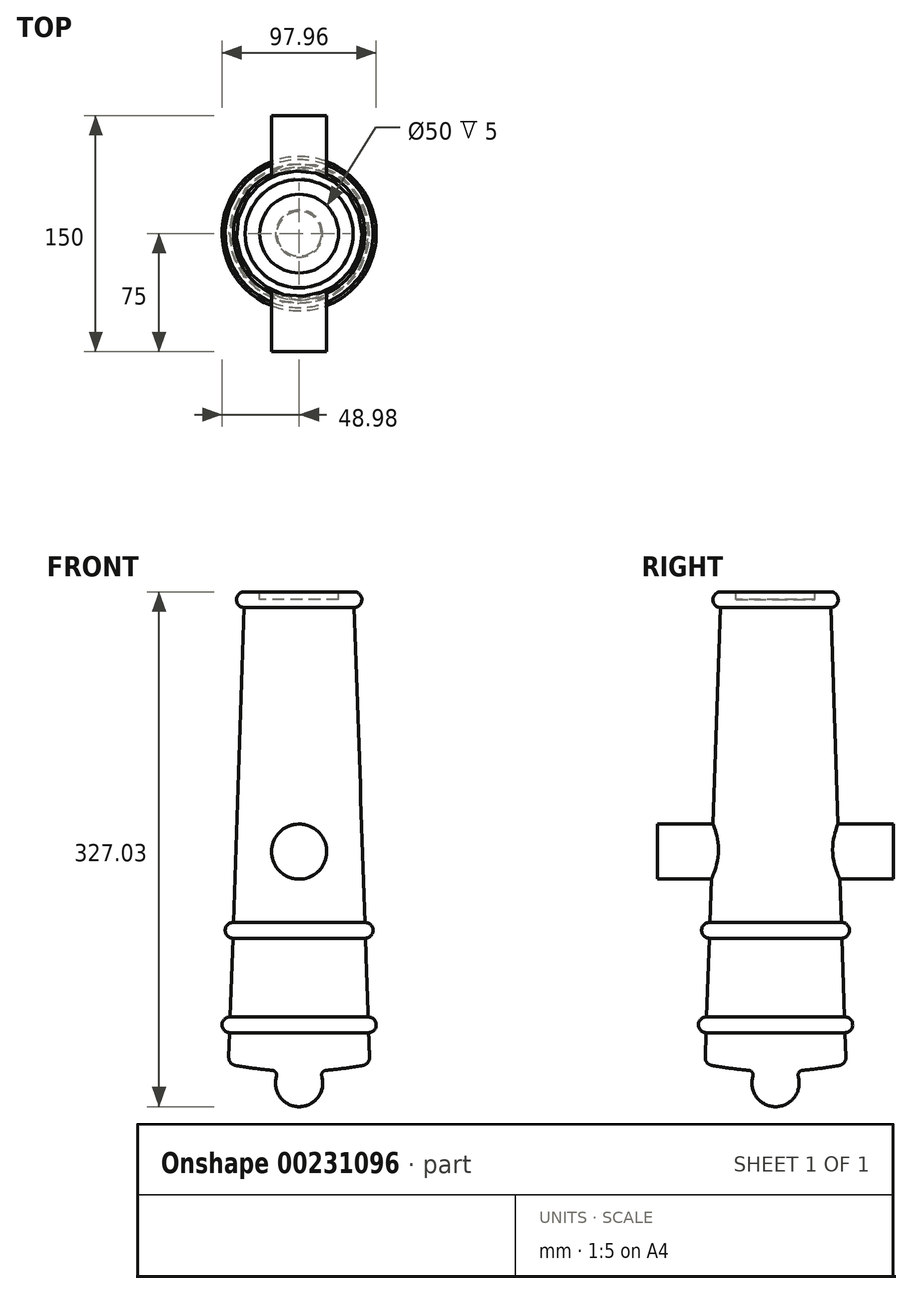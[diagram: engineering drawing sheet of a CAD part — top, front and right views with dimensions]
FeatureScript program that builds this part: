
annotation { "Feature Type Name" : "Feature", "Feature Type Description" : "" }
export const myFeature = defineFeature(function(context is Context, id is Id, definition is map)
    precondition{}
    {
        {
            var Q0;
            Q0=qCreatedBy(makeId("Front.planeOp"),FACE);
            var sketch = newSketch(context, id + "F0", { "sketchPlane" : qUnion([Q0])});
            skLineSegment(sketch, "E0", {"start": v(0, 300) * mm, "end": v(25, 300) * mm});
            skLineSegment(sketch, "E1", {"start": v(25, 300) * mm, "end": v(25, 305) * mm});
            skLineSegment(sketch, "E2", {"start": v(35, 295.03) * mm, "end": v(44.68, 9.3) * mm});
            skArc(sketch, "E3", {"start": v(17, 1.05) * mm, "mid": v(28.81, 2.39) * mm, "end": v(40.56, 4.21) * mm});
            skPoint(sketch, "E4.orphan", {"position": v(45, 0) * mm});
            skPoint(sketch, "E5.visualSharp", {"position": v(44.83, 5) * mm});
            skArc(sketch, "E5.filletArc", {"start": v(40.56, 4.21) * mm, "mid": v(43.57, 5.99) * mm, "end": v(44.68, 9.3) * mm});
            skLineSegment(sketch, "E6", {"start": v(0, 300) * mm, "end": v(0, 0) * mm});
            skCircle(sketch, "E7", {"center": v(43.98, 30) * mm, "radius": 5 * mm});
            skCircle(sketch, "E8", {"center": v(41.95, 90) * mm, "radius": 5 * mm});
            skArc(sketch, "E9", {"start": v(35, 295.03) * mm, "mid": v(39.82, 300.36) * mm, "end": v(34.33, 305) * mm});
            skLineSegment(sketch, "E10", {"start": v(35.34, 305) * mm, "end": v(25, 305) * mm});
            skPoint(sketch, "E11.end.orphan", {"position": v(34.83, 310.5) * mm});
            skLineSegment(sketch, "E12", {"start": v(0, 0) * mm, "end": v(0, -22) * mm});
            skArc(sketch, "E13", {"start": v(0, -22) * mm, "mid": v(12, -16) * mm, "end": v(14.4, -2.78) * mm});
            skPoint(sketch, "E14.visualSharp", {"position": v(12.87, 0.7) * mm});
            skArc(sketch, "E14.filletArc", {"start": v(17, 1.05) * mm, "mid": v(14.8, -0.25) * mm, "end": v(14.4, -2.78) * mm});
            skSolve(sketch);
        }
        {
            var Q0;
            Q0 = qSketchRegion(id + "F0", true);
            var Q1;
            Q1=sQuery(id+"F0.wireOp",EDGE,"E6");
            revolve(context, id + "F1", {"entities" : qUnion([Q0]), "axis" : qUnion([Q1]), "revolveType" : RevolveType.FULL});
        }
        {
            var Q0;
            Q0=qCreatedBy(makeId("Front.planeOp"),FACE);
            var sketch = newSketch(context, id + "F2", { "sketchPlane" : qUnion([Q0])});
            skCircle(sketch, "E15", {"center": v(0, 140) * mm, "radius": 17.5 * mm});
            skSolve(sketch);
        }
        {
            var Q0;
            Q0 = qSketchRegion(id + "F2", true);
            extrude(context, id + "F3", {"entities" : qUnion([Q0]), "operationType" : NewBodyOperationType.ADD, "depth" : 75 * mm, "hasSecondDirection" : true, "secondDirectionOppositeDirection" : true, "secondDirectionDepth" : 75 * mm});
        }
    });
